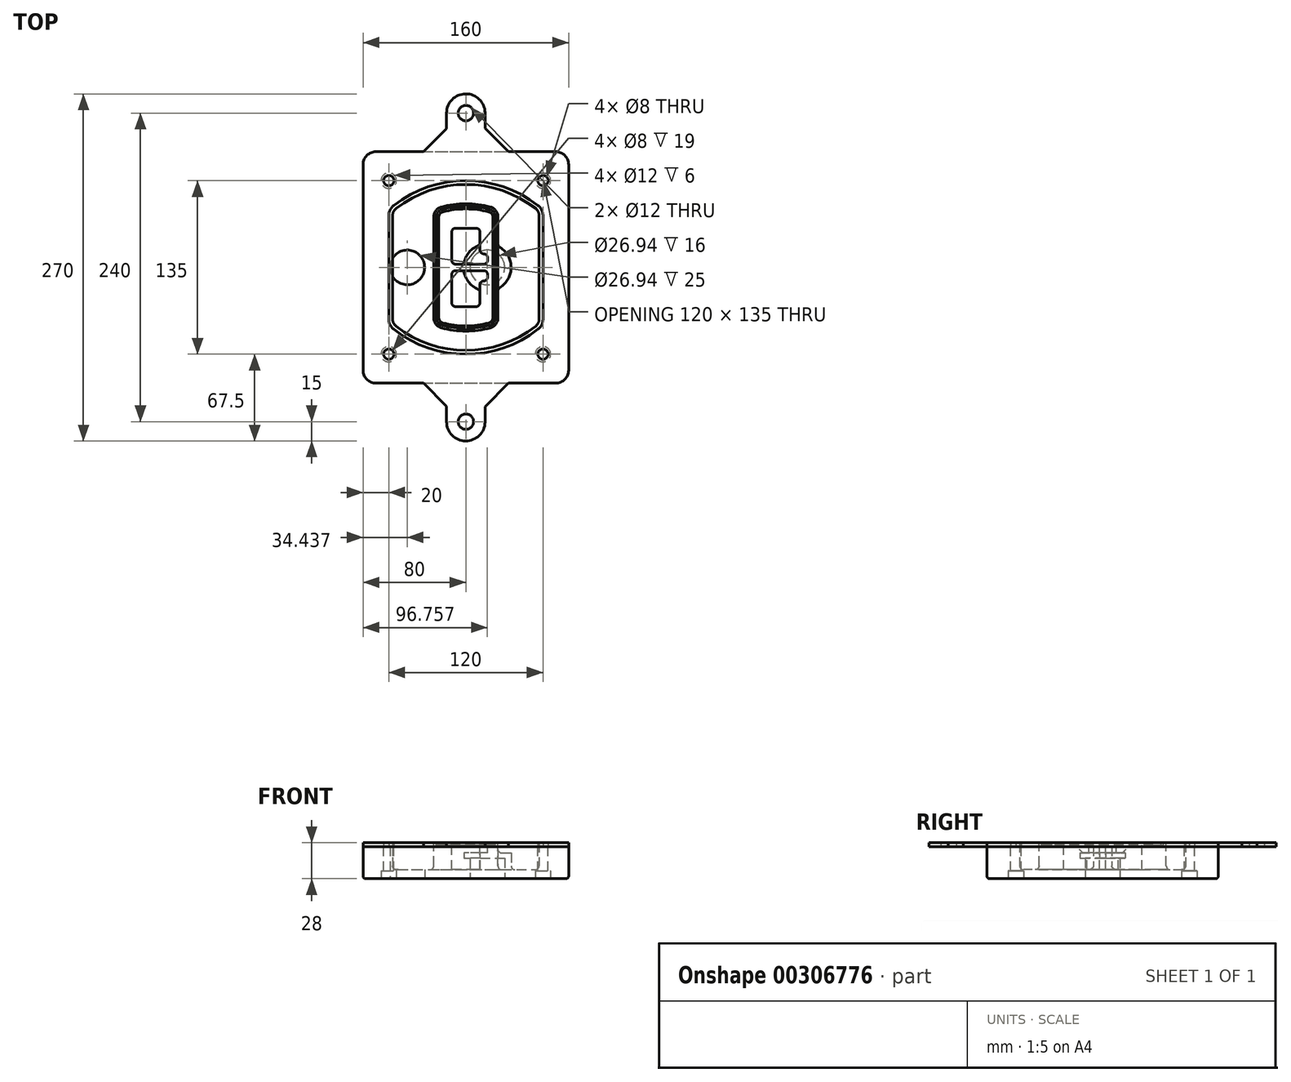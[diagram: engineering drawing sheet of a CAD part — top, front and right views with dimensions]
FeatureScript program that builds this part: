
annotation { "Feature Type Name" : "Feature", "Feature Type Description" : "" }
export const myFeature = defineFeature(function(context is Context, id is Id, definition is map)
    precondition{}
    {
        {
            var Q0;
            Q0=qCreatedBy(makeId("Top.planeOp"),FACE);
            var sketch = newSketch(context, id + "F0", { "sketchPlane" : qUnion([Q0])});
            skPoint(sketch, "E0.rect.middle", {"position": v(0, 0) * mm});
            skLineSegment(sketch, "E1.bottom", {"start": v(-70, -90) * mm, "end": v(70, -90) * mm});
            skLineSegment(sketch, "E1.top", {"start": v(-70, 90) * mm, "end": v(70, 90) * mm});
            skLineSegment(sketch, "E1.left", {"start": v(-80, -80) * mm, "end": v(-80, 80) * mm});
            skLineSegment(sketch, "E1.right", {"start": v(80, -80) * mm, "end": v(80, 80) * mm});
            skLineSegment(sketch, "E2", {"start": v(-80, 90) * mm, "end": v(80, -90) * mm, "construction": true});
            skLineSegment(sketch, "E3", {"start": v(80, 90) * mm, "end": v(-80, -90) * mm, "construction": true});
            skCircle(sketch, "E4", {"center": v(-60, 67.5) * mm, "radius": 4 * mm});
            skCircle(sketch, "E5", {"center": v(60, 67.5) * mm, "radius": 4 * mm});
            skCircle(sketch, "E6", {"center": v(60, -67.5) * mm, "radius": 4 * mm});
            skCircle(sketch, "E7", {"center": v(-60, -67.5) * mm, "radius": 4 * mm});
            skLineSegment(sketch, "E8", {"start": v(-60, 67.5) * mm, "end": v(60, 67.5) * mm, "construction": true});
            skLineSegment(sketch, "E9", {"start": v(60, 67.5) * mm, "end": v(60, -67.5) * mm, "construction": true});
            skLineSegment(sketch, "E10", {"start": v(60, -67.5) * mm, "end": v(-60, -67.5) * mm, "construction": true});
            skLineSegment(sketch, "E11", {"start": v(-60, -67.5) * mm, "end": v(-60, 67.5) * mm, "construction": true});
            skLineSegment(sketch, "E12", {"start": v(-60, 40.3) * mm, "end": v(-60, -40.3) * mm});
            skLineSegment(sketch, "E13", {"start": v(60, 40.3) * mm, "end": v(60, -40.3) * mm});
            skArc(sketch, "E14", {"start": v(56.15, 48.18) * mm, "mid": v(0, 67.5) * mm, "end": v(-56.15, 48.18) * mm});
            skArc(sketch, "E15", {"start": v(-56.15, -48.18) * mm, "mid": v(0, -67.5) * mm, "end": v(56.15, -48.18) * mm});
            skLineSegment(sketch, "E16", {"start": v(-60, 0) * mm, "end": v(60, 0) * mm, "construction": true});
            skPoint(sketch, "E17.visualSharp", {"position": v(-60, -45) * mm});
            skArc(sketch, "E17.filletArc", {"start": v(-60, -40.3) * mm, "mid": v(-58.99, -44.68) * mm, "end": v(-56.15, -48.18) * mm});
            skPoint(sketch, "E18.visualSharp", {"position": v(-60, 45) * mm});
            skArc(sketch, "E18.filletArc", {"start": v(-56.15, 48.18) * mm, "mid": v(-58.99, 44.68) * mm, "end": v(-60, 40.3) * mm});
            skPoint(sketch, "E19.visualSharp", {"position": v(60, 45) * mm});
            skArc(sketch, "E19.filletArc", {"start": v(60, 40.3) * mm, "mid": v(58.99, 44.68) * mm, "end": v(56.15, 48.18) * mm});
            skPoint(sketch, "E20.visualSharp", {"position": v(60, -45) * mm});
            skArc(sketch, "E20.filletArc", {"start": v(56.15, -48.18) * mm, "mid": v(58.99, -44.68) * mm, "end": v(60, -40.3) * mm});
            skPoint(sketch, "E21.visualSharp", {"position": v(-80, 90) * mm});
            skArc(sketch, "E21.filletArc", {"start": v(-70, 90) * mm, "mid": v(-77.07, 87.07) * mm, "end": v(-80, 80) * mm});
            skPoint(sketch, "E22.visualSharp", {"position": v(80, 90) * mm});
            skArc(sketch, "E22.filletArc", {"start": v(80, 80) * mm, "mid": v(77.07, 87.07) * mm, "end": v(70, 90) * mm});
            skPoint(sketch, "E23.visualSharp", {"position": v(80, -90) * mm});
            skArc(sketch, "E23.filletArc", {"start": v(70, -90) * mm, "mid": v(77.07, -87.07) * mm, "end": v(80, -80) * mm});
            skPoint(sketch, "E24.visualSharp", {"position": v(-80, -90) * mm});
            skArc(sketch, "E24.filletArc", {"start": v(-80, -80) * mm, "mid": v(-77.07, -87.07) * mm, "end": v(-70, -90) * mm});
            skArc(sketch, "E25.0", {"start": v(57, 40.3) * mm, "mid": v(56.3, 43.36) * mm, "end": v(54.3, 45.81) * mm});
            skLineSegment(sketch, "E25.1", {"start": v(57, 40.3) * mm, "end": v(57, -40.3) * mm});
            skArc(sketch, "E25.2", {"start": v(54.3, -45.81) * mm, "mid": v(56.3, -43.36) * mm, "end": v(57, -40.3) * mm});
            skArc(sketch, "E25.3", {"start": v(-54.3, -45.81) * mm, "mid": v(0, -64.5) * mm, "end": v(54.3, -45.81) * mm});
            skArc(sketch, "E25.4", {"start": v(-57, -40.3) * mm, "mid": v(-56.3, -43.36) * mm, "end": v(-54.3, -45.81) * mm});
            skArc(sketch, "E25.5", {"start": v(54.3, 45.81) * mm, "mid": v(0, 64.5) * mm, "end": v(-54.3, 45.81) * mm});
            skLineSegment(sketch, "E25.6", {"start": v(-57, 40.3) * mm, "end": v(-57, -40.3) * mm});
            skArc(sketch, "E25.7", {"start": v(-54.3, 45.81) * mm, "mid": v(-56.3, 43.36) * mm, "end": v(-57, 40.3) * mm});
            skArc(sketch, "E26.0", {"start": v(-58.62, 51.33) * mm, "mid": v(-62.58, 46.43) * mm, "end": v(-64, 40.3) * mm});
            skArc(sketch, "E26.1", {"start": v(58.62, 51.33) * mm, "mid": v(0, 71.5) * mm, "end": v(-58.62, 51.33) * mm});
            skArc(sketch, "E26.2", {"start": v(64, 40.3) * mm, "mid": v(62.58, 46.43) * mm, "end": v(58.62, 51.33) * mm});
            skLineSegment(sketch, "E26.3", {"start": v(64, 40.3) * mm, "end": v(64, -40.3) * mm});
            skArc(sketch, "E26.4", {"start": v(58.62, -51.33) * mm, "mid": v(62.58, -46.43) * mm, "end": v(64, -40.3) * mm});
            skLineSegment(sketch, "E26.5", {"start": v(-64, 40.3) * mm, "end": v(-64, -40.3) * mm});
            skArc(sketch, "E26.6", {"start": v(-58.62, -51.33) * mm, "mid": v(0, -71.5) * mm, "end": v(58.62, -51.33) * mm});
            skArc(sketch, "E26.7", {"start": v(-64, -40.3) * mm, "mid": v(-62.58, -46.43) * mm, "end": v(-58.62, -51.33) * mm});
            skSolve(sketch);
        }
        {
            var Q0;
            Q0=makeQuery(id+"F0.imprint","IMPRINT",FACE,{"disambiguationData":[TD([[makeQuery(id+"F0.imprint","IMPRINT",EDGE,{"derivedFrom":sQuery(id+"F0.wireOp",EDGE,"E1.bottom")}),1.0]])]});
            var Q1;
            Q1=makeQuery(id+"F0.imprint","IMPRINT",FACE,{"disambiguationData":[TD([[makeQuery(id+"F0.imprint","IMPRINT",EDGE,{"derivedFrom":sQuery(id+"F0.wireOp",EDGE,"E12")}),1.0]])]});
            var Q2;
            Q2=makeQuery(id+"F0.imprint","IMPRINT",FACE,{"disambiguationData":[TD([[makeQuery(id+"F0.imprint","IMPRINT",EDGE,{"derivedFrom":sQuery(id+"F0.wireOp",EDGE,"E25.0")}),1.0]])]});
            var Q3;
            Q3=makeQuery(id+"F0.imprint","IMPRINT",FACE,{"disambiguationData":[TD([[makeQuery(id+"F0.imprint","IMPRINT",EDGE,{"derivedFrom":sQuery(id+"F0.wireOp",EDGE,"E12")}),-1.0]])]});
            extrude(context, id + "F1", {"entities" : qUnion([Q0, Q1, Q2, Q3]), "oppositeDirection" : true, "depth" : 25 * mm});
        }
        {
            var Q0;
            Q0=makeQuery(id+"F0.imprint","IMPRINT",FACE,{"disambiguationData":[TD([[makeQuery(id+"F0.imprint","IMPRINT",EDGE,{"derivedFrom":sQuery(id+"F0.wireOp",EDGE,"E12")}),1.0]])]});
            extrude(context, id + "F2", {"entities" : qUnion([Q0]), "operationType" : NewBodyOperationType.ADD, "depth" : 3 * mm});
        }
        {
            var Q0;
            Q0=makeQuery(id+"F0.imprint","IMPRINT",FACE,{"disambiguationData":[TD([[makeQuery(id+"F0.imprint","IMPRINT",EDGE,{"derivedFrom":sQuery(id+"F0.wireOp",EDGE,"E25.0")}),1.0]])]});
            extrude(context, id + "F3", {"entities" : qUnion([Q0]), "operationType" : NewBodyOperationType.REMOVE, "oppositeDirection" : true, "depth" : 18 * mm});
        }
        {
            var Q0;
            Q0=makeQuery(id+"F2.opExtrude","CAP_FACE",FACE,{"disambiguationData":[OSD([sQuery(id+"F0.wireOp",EDGE,"E12"),sQuery(id+"F0.wireOp",EDGE,"E13"),sQuery(id+"F0.wireOp",EDGE,"E14"),sQuery(id+"F0.wireOp",EDGE,"E15"),sQuery(id+"F0.wireOp",EDGE,"E17.filletArc"),sQuery(id+"F0.wireOp",EDGE,"E18.filletArc"),sQuery(id+"F0.wireOp",EDGE,"E19.filletArc"),sQuery(id+"F0.wireOp",EDGE,"E20.filletArc"),sQuery(id+"F0.wireOp",EDGE,"E25.0"),sQuery(id+"F0.wireOp",EDGE,"E25.1"),sQuery(id+"F0.wireOp",EDGE,"E25.2"),sQuery(id+"F0.wireOp",EDGE,"E25.3"),sQuery(id+"F0.wireOp",EDGE,"E25.4"),sQuery(id+"F0.wireOp",EDGE,"E25.5"),sQuery(id+"F0.wireOp",EDGE,"E25.6"),sQuery(id+"F0.wireOp",EDGE,"E25.7")])],"isStart":false});
            var sketch = newSketch(context, id + "F4", { "sketchPlane" : qUnion([Q0])});
            skArc(sketch, "E27.0", {"start": v(-19.08, -46.97) * mm, "mid": v(0, -49.5) * mm, "end": v(19.08, -46.97) * mm});
            skArc(sketch, "E28.0", {"start": v(19.08, 46.97) * mm, "mid": v(0, 49.5) * mm, "end": v(-19.08, 46.97) * mm});
            skLineSegment(sketch, "E29", {"start": v(-25, 39.25) * mm, "end": v(-25, -39.25) * mm});
            skLineSegment(sketch, "E30", {"start": v(25, 39.25) * mm, "end": v(25, -39.25) * mm});
            skLineSegment(sketch, "E31", {"start": v(-25, 45.1) * mm, "end": v(25, 45.1) * mm, "construction": true});
            skLineSegment(sketch, "E32", {"start": v(-25, -45.1) * mm, "end": v(25, -45.1) * mm, "construction": true});
            skPoint(sketch, "E33.visualSharp", {"position": v(-25, 45.1) * mm});
            skArc(sketch, "E33.filletArc", {"start": v(-19.08, 46.97) * mm, "mid": v(-23.35, 44.11) * mm, "end": v(-25, 39.25) * mm});
            skPoint(sketch, "E34.visualSharp", {"position": v(25, 45.1) * mm});
            skArc(sketch, "E34.filletArc", {"start": v(25, 39.25) * mm, "mid": v(23.35, 44.11) * mm, "end": v(19.08, 46.97) * mm});
            skPoint(sketch, "E35.visualSharp", {"position": v(25, -45.1) * mm});
            skArc(sketch, "E35.filletArc", {"start": v(19.08, -46.97) * mm, "mid": v(23.35, -44.11) * mm, "end": v(25, -39.25) * mm});
            skPoint(sketch, "E36.visualSharp", {"position": v(-25, -45.1) * mm});
            skArc(sketch, "E36.filletArc", {"start": v(-25, -39.25) * mm, "mid": v(-23.35, -44.11) * mm, "end": v(-19.08, -46.97) * mm});
            skArc(sketch, "E37.0", {"start": v(54.3, 45.81) * mm, "mid": v(0, 64.5) * mm, "end": v(-54.3, 45.81) * mm});
            skArc(sketch, "E37.1", {"start": v(-54.3, 45.81) * mm, "mid": v(-56.3, 43.36) * mm, "end": v(-57, 40.3) * mm});
            skLineSegment(sketch, "E37.2", {"start": v(-57, 40.3) * mm, "end": v(-57, -40.3) * mm});
            skArc(sketch, "E37.3", {"start": v(-57, -40.3) * mm, "mid": v(-56.3, -43.36) * mm, "end": v(-54.3, -45.81) * mm});
            skArc(sketch, "E37.4", {"start": v(-54.3, -45.81) * mm, "mid": v(0, -64.5) * mm, "end": v(54.3, -45.81) * mm});
            skArc(sketch, "E37.5", {"start": v(54.3, -45.81) * mm, "mid": v(56.3, -43.36) * mm, "end": v(57, -40.3) * mm});
            skLineSegment(sketch, "E37.6", {"start": v(57, 40.3) * mm, "end": v(57, -40.3) * mm});
            skArc(sketch, "E37.7", {"start": v(57, 40.3) * mm, "mid": v(56.3, 43.36) * mm, "end": v(54.3, 45.81) * mm});
            skLineSegment(sketch, "E38.0", {"start": v(23, 39.25) * mm, "end": v(23, -39.25) * mm});
            skArc(sketch, "E38.1", {"start": v(18.56, -45.04) * mm, "mid": v(21.76, -42.9) * mm, "end": v(23, -39.25) * mm});
            skArc(sketch, "E38.2", {"start": v(-18.56, -45.04) * mm, "mid": v(0, -47.5) * mm, "end": v(18.56, -45.04) * mm});
            skArc(sketch, "E38.3", {"start": v(-23, -39.25) * mm, "mid": v(-21.76, -42.9) * mm, "end": v(-18.56, -45.04) * mm});
            skLineSegment(sketch, "E38.4", {"start": v(-23, 39.25) * mm, "end": v(-23, -39.25) * mm});
            skArc(sketch, "E38.5", {"start": v(23, 39.25) * mm, "mid": v(21.76, 42.9) * mm, "end": v(18.56, 45.04) * mm});
            skArc(sketch, "E38.6", {"start": v(-18.56, 45.04) * mm, "mid": v(-21.76, 42.9) * mm, "end": v(-23, 39.25) * mm});
            skArc(sketch, "E38.7", {"start": v(18.56, 45.04) * mm, "mid": v(0, 47.5) * mm, "end": v(-18.56, 45.04) * mm});
            skArc(sketch, "E39.0", {"start": v(21, 39.25) * mm, "mid": v(20.18, 41.68) * mm, "end": v(18.04, 43.1) * mm});
            skLineSegment(sketch, "E39.1", {"start": v(21, 39.25) * mm, "end": v(21, -39.25) * mm});
            skArc(sketch, "E39.2", {"start": v(18.04, -43.1) * mm, "mid": v(20.18, -41.68) * mm, "end": v(21, -39.25) * mm});
            skArc(sketch, "E39.3", {"start": v(-18.04, -43.1) * mm, "mid": v(0, -45.5) * mm, "end": v(18.04, -43.1) * mm});
            skArc(sketch, "E39.4", {"start": v(-21, -39.25) * mm, "mid": v(-20.18, -41.68) * mm, "end": v(-18.04, -43.1) * mm});
            skArc(sketch, "E39.5", {"start": v(18.04, 43.1) * mm, "mid": v(0, 45.5) * mm, "end": v(-18.04, 43.1) * mm});
            skLineSegment(sketch, "E39.6", {"start": v(-21, 39.25) * mm, "end": v(-21, -39.25) * mm});
            skArc(sketch, "E39.7", {"start": v(-18.04, 43.1) * mm, "mid": v(-20.18, 41.68) * mm, "end": v(-21, 39.25) * mm});
            skLineSegment(sketch, "E40", {"start": v(-25, 0) * mm, "end": v(25, 0) * mm, "construction": true});
            skLineSegment(sketch, "E41", {"start": v(-11, 5.5) * mm, "end": v(-11, 27.5) * mm});
            skLineSegment(sketch, "E42", {"start": v(-8, 30.5) * mm, "end": v(8, 30.5) * mm});
            skLineSegment(sketch, "E43", {"start": v(11, 27.5) * mm, "end": v(11, 13.5) * mm});
            skLineSegment(sketch, "E44", {"start": v(14, 10.5) * mm, "end": v(14, 10.5) * mm});
            skLineSegment(sketch, "E45", {"start": v(17, 7.5) * mm, "end": v(17, 5.5) * mm});
            skLineSegment(sketch, "E46", {"start": v(14, 2.5) * mm, "end": v(-8, 2.5) * mm});
            skPoint(sketch, "E47.visualSharp", {"position": v(-11, 30.5) * mm});
            skArc(sketch, "E47.filletArc", {"start": v(-8, 30.5) * mm, "mid": v(-10.12, 29.62) * mm, "end": v(-11, 27.5) * mm});
            skPoint(sketch, "E48.visualSharp", {"position": v(11, 30.5) * mm});
            skArc(sketch, "E48.filletArc", {"start": v(11, 27.5) * mm, "mid": v(10.12, 29.62) * mm, "end": v(8, 30.5) * mm});
            skPoint(sketch, "E49.visualSharp", {"position": v(11, 10.5) * mm});
            skArc(sketch, "E49.filletArc", {"start": v(11, 13.5) * mm, "mid": v(11.88, 11.38) * mm, "end": v(14, 10.5) * mm});
            skPoint(sketch, "E50.visualSharp", {"position": v(17, 10.5) * mm});
            skArc(sketch, "E50.filletArc", {"start": v(17, 7.5) * mm, "mid": v(16.12, 9.62) * mm, "end": v(14, 10.5) * mm});
            skPoint(sketch, "E51.visualSharp", {"position": v(17, 2.5) * mm});
            skArc(sketch, "E51.filletArc", {"start": v(14, 2.5) * mm, "mid": v(16.12, 3.38) * mm, "end": v(17, 5.5) * mm});
            skPoint(sketch, "E52.visualSharp", {"position": v(-11, 2.5) * mm});
            skArc(sketch, "E52.filletArc", {"start": v(-11, 5.5) * mm, "mid": v(-10.12, 3.38) * mm, "end": v(-8, 2.5) * mm});
            skLineSegment(sketch, "E53.0.MirrorCS", {"start": v(14, -2.5) * mm, "end": v(-8, -2.5) * mm});
            skArc(sketch, "E54.0.MirrorCS", {"start": v(-11, -5.5) * mm, "mid": v(-10.12, -3.38) * mm, "end": v(-8, -2.5) * mm});
            skLineSegment(sketch, "E55.0.MirrorCS", {"start": v(-11, -5.5) * mm, "end": v(-11, -27.5) * mm});
            skArc(sketch, "E56.0.MirrorCS", {"start": v(-8, -30.5) * mm, "mid": v(-10.12, -29.62) * mm, "end": v(-11, -27.5) * mm});
            skLineSegment(sketch, "E57.0.MirrorCS", {"start": v(-8, -30.5) * mm, "end": v(8, -30.5) * mm});
            skArc(sketch, "E58.0.MirrorCS", {"start": v(11, -27.5) * mm, "mid": v(10.12, -29.62) * mm, "end": v(8, -30.5) * mm});
            skLineSegment(sketch, "E59.0.MirrorCS", {"start": v(11, -27.5) * mm, "end": v(11, -13.5) * mm});
            skArc(sketch, "E60.0.MirrorCS", {"start": v(11, -13.5) * mm, "mid": v(11.88, -11.38) * mm, "end": v(14, -10.5) * mm});
            skArc(sketch, "E61.0.MirrorCS", {"start": v(17, -7.5) * mm, "mid": v(16.12, -9.62) * mm, "end": v(14, -10.5) * mm});
            skLineSegment(sketch, "E62.0.MirrorCS", {"start": v(17, -7.5) * mm, "end": v(17, -5.5) * mm});
            skArc(sketch, "E63.0.MirrorCS", {"start": v(14, -2.5) * mm, "mid": v(16.12, -3.38) * mm, "end": v(17, -5.5) * mm});
            skSolve(sketch);
        }
        {
            var Q0;
            Q0=makeQuery(id+"F4.imprint","IMPRINT",FACE,{"disambiguationData":[TD([[makeQuery(id+"F4.imprint","IMPRINT",EDGE,{"derivedFrom":sQuery(id+"F4.wireOp",EDGE,"E27.0")}),1.0]])]});
            var Q1;
            Q1=makeQuery(id+"F4.imprint","IMPRINT",FACE,{"disambiguationData":[TD([[makeQuery(id+"F4.imprint","IMPRINT",EDGE,{"derivedFrom":sQuery(id+"F4.wireOp",EDGE,"E38.0")}),-1.0]])]});
            var Q2;
            Q2=makeQuery(id+"F4.imprint","IMPRINT",FACE,{"disambiguationData":[TD([[makeQuery(id+"F4.imprint","IMPRINT",EDGE,{"derivedFrom":sQuery(id+"F4.wireOp",EDGE,"E39.0")}),1.0]])]});
            extrude(context, id + "F5", {"entities" : qUnion([Q0, Q1, Q2]), "operationType" : NewBodyOperationType.ADD, "endBound" : BoundingType.UP_TO_NEXT, "oppositeDirection" : true, "depth" : 25 * mm});
        }
        {
            var Q0;
            Q0=makeQuery(id+"F4.imprint","IMPRINT",FACE,{"disambiguationData":[TD([[makeQuery(id+"F4.imprint","IMPRINT",EDGE,{"derivedFrom":sQuery(id+"F4.wireOp",EDGE,"E38.0")}),-1.0]])]});
            extrude(context, id + "F6", {"entities" : qUnion([Q0]), "operationType" : NewBodyOperationType.REMOVE, "oppositeDirection" : true, "depth" : 2 * mm});
        }
        {
            var Q0;
            Q0=makeQuery(id+"F1.opExtrude","CAP_FACE",FACE,{"disambiguationData":[OSD([sQuery(id+"F0.wireOp",EDGE,"E1.bottom"),sQuery(id+"F0.wireOp",EDGE,"E1.top"),sQuery(id+"F0.wireOp",EDGE,"E1.left"),sQuery(id+"F0.wireOp",EDGE,"E1.right"),sQuery(id+"F0.wireOp",EDGE,"E4"),sQuery(id+"F0.wireOp",EDGE,"E5"),sQuery(id+"F0.wireOp",EDGE,"E6"),sQuery(id+"F0.wireOp",EDGE,"E7"),sQuery(id+"F0.wireOp",EDGE,"E21.filletArc"),sQuery(id+"F0.wireOp",EDGE,"E22.filletArc"),sQuery(id+"F0.wireOp",EDGE,"E23.filletArc"),sQuery(id+"F0.wireOp",EDGE,"E24.filletArc")])],"isStart":false});
            var sketch = newSketch(context, id + "F7", { "sketchPlane" : qUnion([Q0])});
            skCircle(sketch, "E64", {"center": v(16.76, 0) * mm, "radius": 13.47 * mm});
            skCircle(sketch, "E65", {"center": v(-45.56, 0) * mm, "radius": 13.47 * mm});
            skLineSegment(sketch, "E66", {"start": v(80, 0) * mm, "end": v(-80, 0) * mm});
            skCircle(sketch, "E67", {"center": v(16.76, 0) * mm, "radius": 18.47 * mm});
            skCircle(sketch, "E68", {"center": v(60, -67.5) * mm, "radius": 6 * mm});
            skCircle(sketch, "E69", {"center": v(-60, -67.5) * mm, "radius": 6 * mm});
            skCircle(sketch, "E70", {"center": v(-60, 67.5) * mm, "radius": 6 * mm});
            skCircle(sketch, "E71", {"center": v(60, 67.5) * mm, "radius": 6 * mm});
            skSolve(sketch);
        }
        {
            var Q0;
            {var subQ1=sQuery(id+"F7.wireOp",EDGE,"E66");var subQ4=sQuery(id+"F7.wireOp",EDGE,"E64");var subQ6=makeQuery(id+"F7.imprint","INTERSECT",VERTEX,{"disambiguationData":[OD(0.0)],"derivedFrom":[subQ4,subQ1]});Q0=makeQuery(id+"F7.imprint","IMPRINT",FACE,{"disambiguationData":[TD([[makeQuery(id+"F7.imprint","IMPRINT",EDGE,{"disambiguationData":[TD([[subQ6,-1.0]])],"derivedFrom":subQ4}),-1.0]])]});}
            var Q1;
            {var subQ0=sQuery(id+"F7.wireOp",EDGE,"E66");var subQ1=sQuery(id+"F7.wireOp",EDGE,"E64");var subQ3=makeQuery(id+"F7.imprint","INTERSECT",VERTEX,{"disambiguationData":[OD(0.0)],"derivedFrom":[subQ1,subQ0]});Q1=makeQuery(id+"F7.imprint","IMPRINT",FACE,{"disambiguationData":[TD([[makeQuery(id+"F7.imprint","IMPRINT",EDGE,{"disambiguationData":[TD([[subQ3,-1.0]])],"derivedFrom":subQ1}),1.0]])]});}
            var Q2;
            {var subQ0=sQuery(id+"F7.wireOp",EDGE,"E66");var subQ1=sQuery(id+"F7.wireOp",EDGE,"E64");var subQ3=makeQuery(id+"F7.imprint","INTERSECT",VERTEX,{"disambiguationData":[OD(0.0)],"derivedFrom":[subQ1,subQ0]});Q2=makeQuery(id+"F7.imprint","IMPRINT",FACE,{"disambiguationData":[TD([[makeQuery(id+"F7.imprint","IMPRINT",EDGE,{"disambiguationData":[TD([[subQ3,1.0]])],"derivedFrom":subQ1}),1.0]])]});}
            var Q3;
            {var subQ1=sQuery(id+"F7.wireOp",EDGE,"E66");var subQ4=sQuery(id+"F7.wireOp",EDGE,"E64");var subQ6=makeQuery(id+"F7.imprint","INTERSECT",VERTEX,{"disambiguationData":[OD(0.0)],"derivedFrom":[subQ4,subQ1]});Q3=makeQuery(id+"F7.imprint","IMPRINT",FACE,{"disambiguationData":[TD([[makeQuery(id+"F7.imprint","IMPRINT",EDGE,{"disambiguationData":[TD([[subQ6,1.0]])],"derivedFrom":subQ4}),-1.0]])]});}
            extrude(context, id + "F8", {"entities" : qUnion([Q0, Q1, Q2, Q3]), "operationType" : NewBodyOperationType.ADD, "oppositeDirection" : true, "depth" : 20 * mm});
        }
        {
            var Q0;
            {var subQ0=sQuery(id+"F7.wireOp",EDGE,"E66");var subQ1=sQuery(id+"F7.wireOp",EDGE,"E64");var subQ3=makeQuery(id+"F7.imprint","INTERSECT",VERTEX,{"disambiguationData":[OD(0.0)],"derivedFrom":[subQ1,subQ0]});Q0=makeQuery(id+"F7.imprint","IMPRINT",FACE,{"disambiguationData":[TD([[makeQuery(id+"F7.imprint","IMPRINT",EDGE,{"disambiguationData":[TD([[subQ3,-1.0]])],"derivedFrom":subQ1}),1.0]])]});}
            var Q1;
            {var subQ0=sQuery(id+"F7.wireOp",EDGE,"E66");var subQ1=sQuery(id+"F7.wireOp",EDGE,"E64");var subQ3=makeQuery(id+"F7.imprint","INTERSECT",VERTEX,{"disambiguationData":[OD(0.0)],"derivedFrom":[subQ1,subQ0]});Q1=makeQuery(id+"F7.imprint","IMPRINT",FACE,{"disambiguationData":[TD([[makeQuery(id+"F7.imprint","IMPRINT",EDGE,{"disambiguationData":[TD([[subQ3,1.0]])],"derivedFrom":subQ1}),1.0]])]});}
            extrude(context, id + "F9", {"entities" : qUnion([Q0, Q1]), "operationType" : NewBodyOperationType.REMOVE, "oppositeDirection" : true, "depth" : 16 * mm});
        }
        {
            var Q0;
            {var subQ0=sQuery(id+"F7.wireOp",EDGE,"E66");var subQ1=sQuery(id+"F7.wireOp",EDGE,"E65");var subQ3=makeQuery(id+"F7.imprint","INTERSECT",VERTEX,{"disambiguationData":[OD(0.0)],"derivedFrom":[subQ1,subQ0]});Q0=makeQuery(id+"F7.imprint","IMPRINT",FACE,{"disambiguationData":[TD([[makeQuery(id+"F7.imprint","IMPRINT",EDGE,{"disambiguationData":[TD([[subQ3,-1.0]])],"derivedFrom":subQ1}),1.0]])]});}
            var Q1;
            {var subQ0=sQuery(id+"F7.wireOp",EDGE,"E66");var subQ1=sQuery(id+"F7.wireOp",EDGE,"E65");var subQ3=makeQuery(id+"F7.imprint","INTERSECT",VERTEX,{"disambiguationData":[OD(0.0)],"derivedFrom":[subQ1,subQ0]});Q1=makeQuery(id+"F7.imprint","IMPRINT",FACE,{"disambiguationData":[TD([[makeQuery(id+"F7.imprint","IMPRINT",EDGE,{"disambiguationData":[TD([[subQ3,1.0]])],"derivedFrom":subQ1}),1.0]])]});}
            extrude(context, id + "F10", {"entities" : qUnion([Q0, Q1]), "operationType" : NewBodyOperationType.REMOVE, "oppositeDirection" : true, "depth" : 25 * mm});
        }
        {
            var Q0;
            Q0=makeQuery(id+"F7.imprint","IMPRINT",FACE,{"disambiguationData":[TD([[makeQuery(id+"F7.imprint","IMPRINT",EDGE,{"derivedFrom":sQuery(id+"F7.wireOp",EDGE,"E68")}),1.0]])]});
            var Q1;
            Q1=makeQuery(id+"F7.imprint","IMPRINT",FACE,{"disambiguationData":[TD([[makeQuery(id+"F7.imprint","IMPRINT",EDGE,{"derivedFrom":makeQuery(id+"F1.opExtrude","CAP_EDGE",EDGE,{"disambiguationData":[OSD([sQuery(id+"F0.wireOp",EDGE,"E5")])],"isStart":false})}),-1.0]])]});
            var Q2;
            Q2=makeQuery(id+"F7.imprint","IMPRINT",FACE,{"disambiguationData":[TD([[makeQuery(id+"F7.imprint","IMPRINT",EDGE,{"derivedFrom":sQuery(id+"F7.wireOp",EDGE,"E69")}),1.0]])]});
            var Q3;
            Q3=makeQuery(id+"F7.imprint","IMPRINT",FACE,{"disambiguationData":[TD([[makeQuery(id+"F7.imprint","IMPRINT",EDGE,{"derivedFrom":makeQuery(id+"F1.opExtrude","CAP_EDGE",EDGE,{"disambiguationData":[OSD([sQuery(id+"F0.wireOp",EDGE,"E4")])],"isStart":false})}),-1.0]])]});
            var Q4;
            Q4=makeQuery(id+"F7.imprint","IMPRINT",FACE,{"disambiguationData":[TD([[makeQuery(id+"F7.imprint","IMPRINT",EDGE,{"derivedFrom":sQuery(id+"F7.wireOp",EDGE,"E70")}),1.0]])]});
            var Q5;
            Q5=makeQuery(id+"F7.imprint","IMPRINT",FACE,{"disambiguationData":[TD([[makeQuery(id+"F7.imprint","IMPRINT",EDGE,{"derivedFrom":makeQuery(id+"F1.opExtrude","CAP_EDGE",EDGE,{"disambiguationData":[OSD([sQuery(id+"F0.wireOp",EDGE,"E7")])],"isStart":false})}),-1.0]])]});
            var Q6;
            Q6=makeQuery(id+"F7.imprint","IMPRINT",FACE,{"disambiguationData":[TD([[makeQuery(id+"F7.imprint","IMPRINT",EDGE,{"derivedFrom":sQuery(id+"F7.wireOp",EDGE,"E71")}),1.0]])]});
            var Q7;
            Q7=makeQuery(id+"F7.imprint","IMPRINT",FACE,{"disambiguationData":[TD([[makeQuery(id+"F7.imprint","IMPRINT",EDGE,{"derivedFrom":makeQuery(id+"F1.opExtrude","CAP_EDGE",EDGE,{"disambiguationData":[OSD([sQuery(id+"F0.wireOp",EDGE,"E6")])],"isStart":false})}),-1.0]])]});
            extrude(context, id + "F11", {"entities" : qUnion([Q0, Q1, Q2, Q3, Q4, Q5, Q6, Q7]), "operationType" : NewBodyOperationType.REMOVE, "oppositeDirection" : true, "depth" : 6 * mm});
        }
        {
            var Q0;
            Q0=makeQuery(id+"F9.boolean.opBoolean","COPY",FACE,{"derivedFrom":makeQuery(id+"F9.opExtrude","CAP_FACE",FACE,{"disambiguationData":[OSD([sQuery(id+"F7.wireOp",EDGE,"E64")])],"isStart":false})});
            var sketch = newSketch(context, id + "F12", { "sketchPlane" : qUnion([Q0])});
            skArc(sketch, "E72.0", {"start": v(11, 17.55) * mm, "mid": v(2.57, 11.82) * mm, "end": v(-1.54, 2.5) * mm});
            skArc(sketch, "E72.1", {"start": v(-1.54, -2.5) * mm, "mid": v(2.57, -11.82) * mm, "end": v(11, -17.55) * mm});
            skLineSegment(sketch, "E73", {"start": v(-1.54, -2.5) * mm, "end": v(14, -2.5) * mm});
            skLineSegment(sketch, "E74.0", {"start": v(14, 2.5) * mm, "end": v(-1.54, 2.5) * mm});
            skArc(sketch, "E74.1", {"start": v(14, 2.5) * mm, "mid": v(16.12, 3.38) * mm, "end": v(17, 5.5) * mm});
            skLineSegment(sketch, "E74.2", {"start": v(17, 7.5) * mm, "end": v(17, 5.5) * mm});
            skArc(sketch, "E74.3", {"start": v(17, 7.5) * mm, "mid": v(16.12, 9.62) * mm, "end": v(14, 10.5) * mm});
            skArc(sketch, "E74.4", {"start": v(11, 13.5) * mm, "mid": v(11.88, 11.38) * mm, "end": v(14, 10.5) * mm});
            skLineSegment(sketch, "E74.5", {"start": v(11, 17.55) * mm, "end": v(11, 13.5) * mm});
            skLineSegment(sketch, "E74.7", {"start": v(14, -2.5) * mm, "end": v(-1.54, -2.5) * mm});
            skArc(sketch, "E74.8", {"start": v(14, -2.5) * mm, "mid": v(16.12, -3.38) * mm, "end": v(17, -5.5) * mm});
            skLineSegment(sketch, "E74.9", {"start": v(17, -7.5) * mm, "end": v(17, -5.5) * mm});
            skArc(sketch, "E74.10", {"start": v(17, -7.5) * mm, "mid": v(16.12, -9.62) * mm, "end": v(14, -10.5) * mm});
            skArc(sketch, "E74.11", {"start": v(11, -13.5) * mm, "mid": v(11.88, -11.38) * mm, "end": v(14, -10.5) * mm});
            skLineSegment(sketch, "E74.12", {"start": v(11, -17.55) * mm, "end": v(11, -13.5) * mm});
            skPoint(sketch, "E75.orphan", {"position": v(11, -27.5) * mm});
            skPoint(sketch, "E76.orphan", {"position": v(-8, -2.5) * mm});
            skPoint(sketch, "E77.orphan", {"position": v(-8, 2.5) * mm});
            skPoint(sketch, "E78.orphan", {"position": v(11, 27.5) * mm});
            skSolve(sketch);
        }
        {
            var Q0;
            {var subQ7=sQuery(id+"F12.wireOp",EDGE,"E72.0");var subQ14=sQuery(id+"F12.wireOp",EDGE,"E72.1");var subQ16=sQuery(id+"F12.wireOp",EDGE,"E74.1");var subQ18=sQuery(id+"F12.wireOp",EDGE,"E74.8");Q0=qUnion([makeQuery(id+"F12.imprint","IMPRINT",FACE,{"disambiguationData":[TD([[makeQuery(id+"F12.imprint","IMPRINT",EDGE,{"derivedFrom":subQ7}),1.0]])]}),makeQuery(id+"F12.imprint","IMPRINT",FACE,{"disambiguationData":[TD([[makeQuery(id+"F12.imprint","IMPRINT",EDGE,{"derivedFrom":subQ14}),1.0]])]}),makeQuery(id+"F12.imprint","IMPRINT",FACE,{"disambiguationData":[TD([[makeQuery(id+"F12.imprint","IMPRINT",EDGE,{"derivedFrom":subQ16}),1.0]])]}),makeQuery(id+"F12.imprint","IMPRINT",FACE,{"disambiguationData":[TD([[makeQuery(id+"F12.imprint","IMPRINT",EDGE,{"derivedFrom":subQ18}),-1.0]])]})]);}
            var Q1;
            Q1=makeQuery(id+"F5.boolean.opBoolean","SPLIT",FACE,{"disambiguationData":[TD([makeQuery(id+"F5.opExtrude","SWEPT_FACE",FACE,{"disambiguationData":[OSD([sQuery(id+"F4.wireOp",EDGE,"E41")])]})])],"derivedFrom":makeQuery(id+"F3.boolean.opBoolean","COPY",FACE,{"derivedFrom":makeQuery(id+"F3.opExtrude","CAP_FACE",FACE,{"disambiguationData":[OSD([sQuery(id+"F0.wireOp",EDGE,"E25.0"),sQuery(id+"F0.wireOp",EDGE,"E25.1"),sQuery(id+"F0.wireOp",EDGE,"E25.2"),sQuery(id+"F0.wireOp",EDGE,"E25.3"),sQuery(id+"F0.wireOp",EDGE,"E25.4"),sQuery(id+"F0.wireOp",EDGE,"E25.5"),sQuery(id+"F0.wireOp",EDGE,"E25.6"),sQuery(id+"F0.wireOp",EDGE,"E25.7")])],"isStart":false})})});
            extrude(context, id + "F13", {"entities" : qUnion([Q0]), "operationType" : NewBodyOperationType.REMOVE, "endBound" : BoundingType.UP_TO_SURFACE, "endBoundEntityFace" : qUnion([Q1]), "depth" : 25 * mm});
        }
        {
            var Q0;
            Q0=makeQuery(id+"F3.boolean.opBoolean","COPY",EDGE,{"derivedFrom":makeQuery(id+"F3.opExtrude","CAP_EDGE",EDGE,{"disambiguationData":[OSD([sQuery(id+"F0.wireOp",EDGE,"E25.6")])],"isStart":false})});
            var Q1;
            Q1=makeQuery(id+"F8.boolean.opBoolean","INTERSECT",EDGE,{"derivedFrom":[makeQuery(id+"F5.opExtrude","SWEPT_FACE",FACE,{"disambiguationData":[OSD([sQuery(id+"F4.wireOp",EDGE,"E30")])]}),makeQuery(id+"F8.opExtrude","CAP_FACE",FACE,{"disambiguationData":[OSD([sQuery(id+"F7.wireOp",EDGE,"E67")])],"isStart":false})]});
            var Q2;
            Q2=makeQuery(id+"F8.boolean.opBoolean","INTERSECT",EDGE,{"disambiguationData":[OD(1.0)],"derivedFrom":[makeQuery(id+"F5.opExtrude","SWEPT_FACE",FACE,{"disambiguationData":[OSD([sQuery(id+"F4.wireOp",EDGE,"E30")])]}),makeQuery(id+"F8.opExtrude","SWEPT_FACE",FACE,{"disambiguationData":[OSD([sQuery(id+"F7.wireOp",EDGE,"E67")])]})]});
            var Q3;
            {var subQ0=sQuery(id+"F4.wireOp",EDGE,"E30");Q3=makeQuery(id+"F8.boolean.opBoolean","SPLIT",EDGE,{"disambiguationData":[TD([makeQuery(id+"F5.opExtrude","SWEPT_FACE",FACE,{"disambiguationData":[OSD([sQuery(id+"F4.wireOp",EDGE,"E35.filletArc")])]})])],"derivedFrom":makeQuery(id+"F5.opExtrude","CAP_EDGE",EDGE,{"disambiguationData":[OSD([subQ0])],"isStart":false})});}
            var Q4;
            {var subQ0=sQuery(id+"F0.wireOp",EDGE,"E25.7");var subQ1=sQuery(id+"F0.wireOp",EDGE,"E25.1");var subQ2=sQuery(id+"F0.wireOp",EDGE,"E25.6");var subQ3=sQuery(id+"F0.wireOp",EDGE,"E25.5");var subQ4=sQuery(id+"F0.wireOp",EDGE,"E25.4");var subQ5=sQuery(id+"F0.wireOp",EDGE,"E25.0");var subQ6=sQuery(id+"F0.wireOp",EDGE,"E25.2");var subQ7=sQuery(id+"F0.wireOp",EDGE,"E25.3");Q4=makeQuery(id+"F8.boolean.opBoolean","INTERSECT",EDGE,{"derivedFrom":[makeQuery(id+"F5.boolean.opBoolean","SPLIT",FACE,{"disambiguationData":[TD([makeQuery(id+"F2.opExtrude","SWEPT_FACE",FACE,{"disambiguationData":[OSD([subQ5])]})])],"derivedFrom":makeQuery(id+"F3.boolean.opBoolean","COPY",FACE,{"derivedFrom":makeQuery(id+"F3.opExtrude","CAP_FACE",FACE,{"disambiguationData":[OSD([subQ5,subQ1,subQ6,subQ7,subQ4,subQ3,subQ2,subQ0])],"isStart":false})})}),makeQuery(id+"F8.opExtrude","SWEPT_FACE",FACE,{"disambiguationData":[OSD([sQuery(id+"F7.wireOp",EDGE,"E67")])]})]});}
            var Q5;
            Q5=makeQuery(id+"F8.boolean.opBoolean","INTERSECT",EDGE,{"disambiguationData":[OD(0.0)],"derivedFrom":[makeQuery(id+"F5.opExtrude","SWEPT_FACE",FACE,{"disambiguationData":[OSD([sQuery(id+"F4.wireOp",EDGE,"E30")])]}),makeQuery(id+"F8.opExtrude","SWEPT_FACE",FACE,{"disambiguationData":[OSD([sQuery(id+"F7.wireOp",EDGE,"E67")])]})]});
            fillet(context, id + "F14", {"entities" : qUnion([Q0, Q1, Q2, Q3, Q4, Q5]), "radius" : 3 * mm, "tangentPropagation" : true, "allowEdgeOverflow" : false});
        }
        {
            var Q0;
            Q0=makeQuery(id+"F1.opExtrude","CAP_EDGE",EDGE,{"disambiguationData":[OSD([sQuery(id+"F0.wireOp",EDGE,"E1.bottom")])],"isStart":false});
            fillet(context, id + "F15", {"entities" : qUnion([Q0]), "radius" : 2 * mm, "tangentPropagation" : true, "allowEdgeOverflow" : false});
        }
        {
            var Q0;
            {var subQ0=sQuery(id+"F0.wireOp",EDGE,"E21.filletArc");var subQ1=sQuery(id+"F0.wireOp",EDGE,"E7");var subQ2=sQuery(id+"F0.wireOp",EDGE,"E6");var subQ3=sQuery(id+"F0.wireOp",EDGE,"E5");var subQ4=sQuery(id+"F0.wireOp",EDGE,"E4");var subQ5=sQuery(id+"F0.wireOp",EDGE,"E22.filletArc");var subQ6=sQuery(id+"F0.wireOp",EDGE,"E1.bottom");var subQ7=sQuery(id+"F0.wireOp",EDGE,"E1.right");var subQ8=sQuery(id+"F0.wireOp",EDGE,"E1.top");var subQ9=sQuery(id+"F0.wireOp",EDGE,"E1.left");var subQ10=sQuery(id+"F0.wireOp",EDGE,"E23.filletArc");var subQ11=sQuery(id+"F0.wireOp",EDGE,"E24.filletArc");Q0=makeQuery(id+"F2.boolean.opBoolean","SPLIT",FACE,{"disambiguationData":[TD([makeQuery(id+"F1.opExtrude","SWEPT_FACE",FACE,{"disambiguationData":[OSD([subQ6])]})])],"derivedFrom":makeQuery(id+"F1.opExtrude","CAP_FACE",FACE,{"disambiguationData":[OSD([subQ6,subQ8,subQ9,subQ7,subQ4,subQ3,subQ2,subQ1,subQ0,subQ5,subQ10,subQ11])],"isStart":true})});}
            var sketch = newSketch(context, id + "F16", { "sketchPlane" : qUnion([Q0])});
            skLineSegment(sketch, "E79", {"start": v(-33, 90) * mm, "end": v(-15, 108) * mm});
            skLineSegment(sketch, "E80", {"start": v(-15, 108) * mm, "end": v(-15, 120) * mm});
            skArc(sketch, "E81", {"start": v(15, 120.3) * mm, "mid": v(-0.15, 135) * mm, "end": v(-15, 120) * mm});
            skLineSegment(sketch, "E82", {"start": v(15, 120.3) * mm, "end": v(15, 108.3) * mm});
            skLineSegment(sketch, "E83", {"start": v(15, 108.3) * mm, "end": v(33.3, 90) * mm});
            skCircle(sketch, "E84", {"center": v(0, 120) * mm, "radius": 6 * mm});
            skLineSegment(sketch, "E85", {"start": v(0, 120) * mm, "end": v(0, 90) * mm, "construction": true});
            skLineSegment(sketch, "E86", {"start": v(-80, 0) * mm, "end": v(80, 0) * mm, "construction": true});
            skArc(sketch, "E87.MirrorCS", {"start": v(15, -120.3) * mm, "mid": v(-0.15, -135) * mm, "end": v(-15, -120) * mm});
            skLineSegment(sketch, "E88.MirrorCS", {"start": v(-15, -108) * mm, "end": v(-15, -120) * mm});
            skLineSegment(sketch, "E89.MirrorCS", {"start": v(-33, -90) * mm, "end": v(-15, -108) * mm});
            skLineSegment(sketch, "E90.MirrorCS", {"start": v(15, -108.3) * mm, "end": v(33.3, -90) * mm});
            skLineSegment(sketch, "E91.MirrorCS", {"start": v(15, -120.3) * mm, "end": v(15, -108.3) * mm});
            skCircle(sketch, "E92.MirrorC", {"center": v(0, -120) * mm, "radius": 6 * mm});
            skLineSegment(sketch, "E93.MirrorCS", {"start": v(0, -120) * mm, "end": v(0, -90) * mm, "construction": true});
            skSolve(sketch);
        }
        {
            var Q0;
            Q0=makeQuery(id+"F16.imprint","IMPRINT",FACE,{"disambiguationData":[TD([[makeQuery(id+"F16.imprint","IMPRINT",EDGE,{"derivedFrom":makeQuery(id+"F1.opExtrude","CAP_EDGE",EDGE,{"disambiguationData":[OSD([sQuery(id+"F0.wireOp",EDGE,"E1.left")])],"isStart":true})}),-1.0]])]});
            var Q1;
            {var subQ0=sQuery(id+"F16.wireOp",EDGE,"E79");Q1=makeQuery(id+"F16.imprint","IMPRINT",FACE,{"disambiguationData":[TD([[makeQuery(id+"F16.imprint","IMPRINT",EDGE,{"derivedFrom":subQ0}),-1.0]])]});}
            var Q2;
            Q2=makeQuery(id+"F16.imprint","IMPRINT",FACE,{"disambiguationData":[TD([[makeQuery(id+"F16.imprint","IMPRINT",EDGE,{"derivedFrom":sQuery(id+"F16.wireOp",EDGE,"E88.MirrorCS")}),1.0]])]});
            var Q3;
            Q3=makeQuery(id+"F2.opExtrude","CAP_FACE",FACE,{"disambiguationData":[OSD([sQuery(id+"F0.wireOp",EDGE,"E12"),sQuery(id+"F0.wireOp",EDGE,"E13"),sQuery(id+"F0.wireOp",EDGE,"E14"),sQuery(id+"F0.wireOp",EDGE,"E15"),sQuery(id+"F0.wireOp",EDGE,"E17.filletArc"),sQuery(id+"F0.wireOp",EDGE,"E18.filletArc"),sQuery(id+"F0.wireOp",EDGE,"E19.filletArc"),sQuery(id+"F0.wireOp",EDGE,"E20.filletArc"),sQuery(id+"F0.wireOp",EDGE,"E25.0"),sQuery(id+"F0.wireOp",EDGE,"E25.1"),sQuery(id+"F0.wireOp",EDGE,"E25.2"),sQuery(id+"F0.wireOp",EDGE,"E25.3"),sQuery(id+"F0.wireOp",EDGE,"E25.4"),sQuery(id+"F0.wireOp",EDGE,"E25.5"),sQuery(id+"F0.wireOp",EDGE,"E25.6"),sQuery(id+"F0.wireOp",EDGE,"E25.7")])],"isStart":false});
            extrude(context, id + "F17", {"entities" : qUnion([Q0, Q1, Q2]), "endBound" : BoundingType.UP_TO_SURFACE, "endBoundEntityFace" : qUnion([Q3]), "depth" : 25 * mm});
        }
    });
